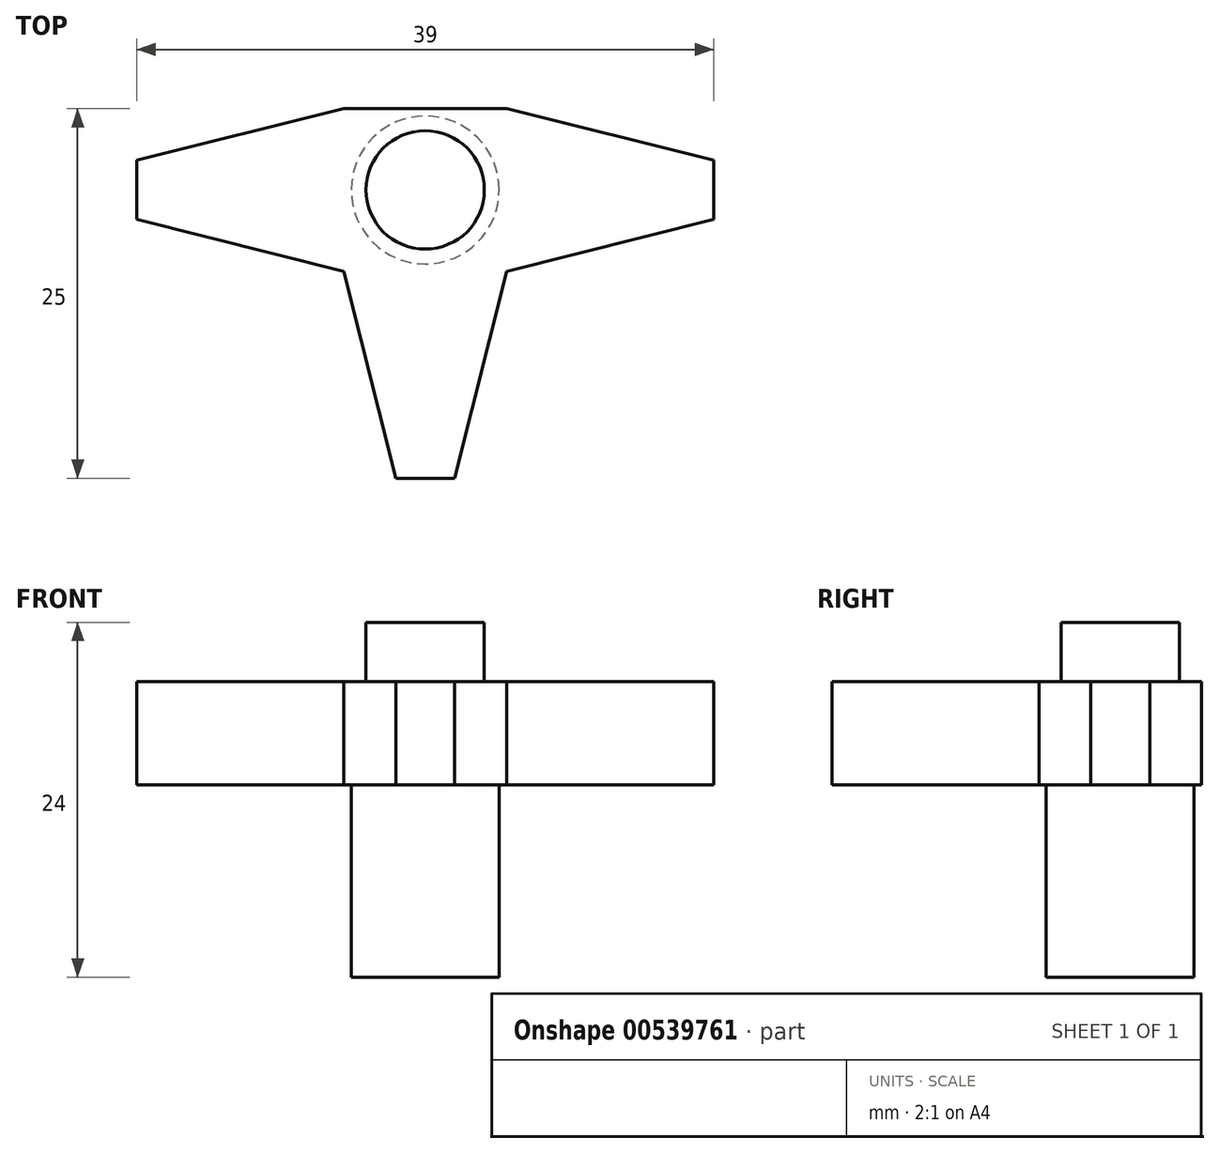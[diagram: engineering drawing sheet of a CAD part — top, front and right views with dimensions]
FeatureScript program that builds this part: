
annotation { "Feature Type Name" : "Feature", "Feature Type Description" : "" }
export const myFeature = defineFeature(function(context is Context, id is Id, definition is map)
    precondition{}
    {
        {
            var Q0;
            Q0=qCreatedBy(makeId("Top.planeOp"),FACE);
            var sketch = newSketch(context, id + "F0", { "sketchPlane" : qUnion([Q0])});
            skLineSegment(sketch, "E0.bottom", {"start": v(5.5, -5.5) * mm, "end": v(-5.5, -5.5) * mm});
            skLineSegment(sketch, "E0.top", {"start": v(5.5, 5.5) * mm, "end": v(-5.5, 5.5) * mm});
            skLineSegment(sketch, "E0.left", {"start": v(5.5, -5.5) * mm, "end": v(5.5, 5.5) * mm});
            skLineSegment(sketch, "E0.right", {"start": v(-5.5, -5.5) * mm, "end": v(-5.5, 5.5) * mm});
            skPoint(sketch, "E0.middle", {"position": v(0, 0) * mm});
            skLineSegment(sketch, "E1", {"start": v(-74.53, 0) * mm, "end": v(74.63, 0) * mm, "construction": true});
            skLineSegment(sketch, "E2", {"start": v(0, 56.37) * mm, "end": v(0, -55.35) * mm, "construction": true});
            skLineSegment(sketch, "E3.bottom", {"start": v(-5.5, 5.5) * mm, "end": v(5.5, 5.5) * mm});
            skLineSegment(sketch, "E3.top", {"start": v(-2, 19.5) * mm, "end": v(2, 19.5) * mm});
            skLineSegment(sketch, "E3.left", {"start": v(-5.5, 5.5) * mm, "end": v(-2, 19.5) * mm});
            skLineSegment(sketch, "E3.right", {"start": v(5.5, 5.5) * mm, "end": v(2, 19.5) * mm});
            skPoint(sketch, "E4", {"position": v(0, 19.5) * mm});
            skLineSegment(sketch, "E5.1.0", {"start": v(-5.5, -5.5) * mm, "end": v(-19.5, -2) * mm});
            skLineSegment(sketch, "E5.1.1", {"start": v(-5.5, 5.5) * mm, "end": v(-19.5, 2) * mm});
            skLineSegment(sketch, "E5.1.2", {"start": v(-19.5, -2) * mm, "end": v(-19.5, 2) * mm});
            skPoint(sketch, "E5.1.3", {"position": v(-19.5, 0) * mm});
            skLineSegment(sketch, "E5.2.0", {"start": v(5.5, -5.5) * mm, "end": v(2, -19.5) * mm});
            skLineSegment(sketch, "E5.2.1", {"start": v(-5.5, -5.5) * mm, "end": v(-2, -19.5) * mm});
            skLineSegment(sketch, "E5.2.2", {"start": v(2, -19.5) * mm, "end": v(-2, -19.5) * mm});
            skPoint(sketch, "E5.2.3", {"position": v(0, -19.5) * mm});
            skLineSegment(sketch, "E5.3.0", {"start": v(5.5, 5.5) * mm, "end": v(19.5, 2) * mm});
            skLineSegment(sketch, "E5.3.1", {"start": v(5.5, -5.5) * mm, "end": v(19.5, -2) * mm});
            skLineSegment(sketch, "E5.3.2", {"start": v(19.5, 2) * mm, "end": v(19.5, -2) * mm});
            skPoint(sketch, "E5.3.3", {"position": v(19.5, 0) * mm});
            skCircle(sketch, "E6", {"center": v(0, 0) * mm, "radius": 5 * mm});
            skSolve(sketch);
        }
        {
            var Q0;
            Q0=makeQuery(id+"F0.imprint","IMPRINT",FACE,{"disambiguationData":[TD([[makeQuery(id+"F0.imprint","IMPRINT",EDGE,{"derivedFrom":sQuery(id+"F0.wireOp",EDGE,"E0.bottom")}),-1.0]])]});
            var Q1;
            Q1=makeQuery(id+"F0.imprint","IMPRINT",FACE,{"disambiguationData":[TD([[makeQuery(id+"F0.imprint","IMPRINT",EDGE,{"derivedFrom":sQuery(id+"F0.wireOp",EDGE,"E6")}),1.0]])]});
            var Q2;
            Q2=makeQuery(id+"F0.imprint","IMPRINT",FACE,{"disambiguationData":[TD([[makeQuery(id+"F0.imprint","IMPRINT",EDGE,{"derivedFrom":sQuery(id+"F0.wireOp",EDGE,"E0.bottom")}),1.0]])]});
            var Q3;
            Q3=makeQuery(id+"F0.imprint","IMPRINT",FACE,{"disambiguationData":[TD([[makeQuery(id+"F0.imprint","IMPRINT",EDGE,{"derivedFrom":sQuery(id+"F0.wireOp",EDGE,"E0.left")}),-1.0]])]});
            var Q4;
            Q4=makeQuery(id+"F0.imprint","IMPRINT",FACE,{"disambiguationData":[TD([[makeQuery(id+"F0.imprint","IMPRINT",EDGE,{"derivedFrom":sQuery(id+"F0.wireOp",EDGE,"E0.right")}),1.0]])]});
            var Q5;
            Q5=makeQuery(id+"F0.imprint","IMPRINT",FACE,{"disambiguationData":[TD([[makeQuery(id+"F0.imprint","IMPRINT",EDGE,{"derivedFrom":sQuery(id+"F0.wireOp",EDGE,"E3.bottom")}),1.0]])]});
            extrude(context, id + "F1", {"entities" : qUnion([Q0, Q1, Q2, Q3, Q4, Q5]), "depth" : 7 * mm, "offsetDistance" : 25 * mm});
        }
        {
            var Q0;
            Q0=makeQuery(id+"F0.imprint","IMPRINT",FACE,{"disambiguationData":[TD([[makeQuery(id+"F0.imprint","IMPRINT",EDGE,{"derivedFrom":sQuery(id+"F0.wireOp",EDGE,"E6")}),1.0]])]});
            extrude(context, id + "F2", {"entities" : qUnion([Q0]), "operationType" : NewBodyOperationType.ADD, "oppositeDirection" : true, "depth" : 13 * mm, "offsetDistance" : 25 * mm});
        }
        {
            var Q0;
            Q0=makeQuery(id+"F1.opExtrude","CAP_FACE",FACE,{"disambiguationData":[OSD([sQuery(id+"F0.wireOp",EDGE,"E3.top"),sQuery(id+"F0.wireOp",EDGE,"E3.left"),sQuery(id+"F0.wireOp",EDGE,"E3.right"),sQuery(id+"F0.wireOp",EDGE,"E5.1.0"),sQuery(id+"F0.wireOp",EDGE,"E5.1.1"),sQuery(id+"F0.wireOp",EDGE,"E5.1.2"),sQuery(id+"F0.wireOp",EDGE,"E5.2.0"),sQuery(id+"F0.wireOp",EDGE,"E5.2.1"),sQuery(id+"F0.wireOp",EDGE,"E5.2.2"),sQuery(id+"F0.wireOp",EDGE,"E5.3.0"),sQuery(id+"F0.wireOp",EDGE,"E5.3.1"),sQuery(id+"F0.wireOp",EDGE,"E5.3.2")])],"isStart":false});
            var sketch = newSketch(context, id + "F3", { "sketchPlane" : qUnion([Q0])});
            skCircle(sketch, "E7", {"center": v(0, 0) * mm, "radius": 4 * mm});
            skSolve(sketch);
        }
        {
            var Q0;
            Q0=makeQuery(id+"F3.imprint","IMPRINT",FACE,{"disambiguationData":[TD([[makeQuery(id+"F3.imprint","IMPRINT",EDGE,{"derivedFrom":sQuery(id+"F3.wireOp",EDGE,"E7")}),1.0]])]});
            extrude(context, id + "F4", {"entities" : qUnion([Q0]), "operationType" : NewBodyOperationType.ADD, "depth" : 4 * mm, "offsetDistance" : 25 * mm});
        }
    });
